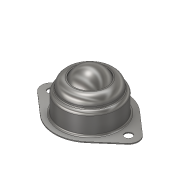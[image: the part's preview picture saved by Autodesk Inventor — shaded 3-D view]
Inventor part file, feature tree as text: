
AUTODESK INVENTOR PART (.ipt)
format: ipt  version: 2019.4 (Build 234330000, 330)  size: 253,440 bytes
history: native  units: in
note: dims shown in document units (in); Inventor stores cm internally (conversion verified against a paired STEP export)
features: revolve x1, shell x1
ambient origin geometry x8: Origin, YZ Plane, XZ Plane, XY Plane, X Axis, Y Axis, Z Axis, Center Point
bodies: Solid1 (feature_tree), Solid2 (feature_tree)
feature tree (2):
  revolve  "Revolve2"  [1 undecoded]
  shell  "Shell1"  [1 undecoded]
note: 2 required parameter values undecoded (feature->parameter linkage not recoverable at this tier; creation-order binding heuristic only, values carry confidence <= 0.55)
